# Revit family: 756-122-143-DN700-1200
name_source: partatom
category: Pipe Accessories
units: mm (PartAtom-declared; Revit-internal decimal feet)

## family parameters
Always vertical = Yes
Cut with Voids When Loaded = No
Part Type = Valve - Breaks Into
Round Connector Dimension = Use Diameter
Shared = No
Work Plane-Based = No

## types (10) — shared parameters
Body_wallthickness = 10 mm  [stored 0.0328084 ft]
D = 240 mm
D1 = 10 mm  [stored 0.0328084 ft]
DN1000-PN10 = 756-1000-1-0402200048
DN1000-PN16 = 756-1000-1-1402200048
DN1200-PN10 = 756-1200-1-0402200048
DN1200-PN16 = 756-1200-1-1402200048
DN700_PN10 = 756-0700-1-0402200048
DN700_PN16 = 756-0700-1-1402200048
DN800_PN10 = 756-0800-1-0402200048
DN800_PN16 = 756-0800-1-1402200048
DN900-PN16 = 756-0900-1-1402200048
DN900_PN10 = 756-0900-1-0402200048
Description_ = AVK DOUBLE ECC. BUTTERFLY VALVE, LONG
Disk_1 = 25 mm  [stored 0.082021 ft]
Disk_2 = 25 mm  [stored 0.082021 ft]
GB_Flange = 5 mm  [stored 0.0164042 ft]
HW_Connecting rod ref = 480 mm
HW_Dia = 20 mm  [stored 0.0656168 ft]
Offset = 3 mm  [stored 0.00984252 ft]
Pin_dia = 60 mm  [stored 0.19685 ft]
RF_Cut_Thickness = 5 mm  [stored 0.0164042 ft]
Rib_depth = 15 mm  [stored 0.0492126 ft]
Search_table = 756-122-143-DN700-1200
URL_product_pages = https://www.avkvalves.com

## per-type parameters (varying)
- DN0700_PN16: A=342 mm; A2=201.18 mm; B=615 mm; Bottom_Depth=1050.15 mm; Bottom_width=427 mm; C=297 mm; C_Rod=38 mm  [stored 0.124672 ft]; DN=700.1 mm; Disc_Dia=684 mm; Disc_width=40 mm  [stored 0.131234 ft]; Flange_OD=455 mm; Flange_Thickness=40 mm  [stored 0.131234 ft]; GB_Dia=39.75 mm  [stored 0.130413 ft]; GB_HW=95 mm; GB_Width=82 mm  [stored 0.269029 ft]; GB_Width_2=117 mm  [stored 0.383858 ft]; GB_Width_3=130 mm  [stored 0.426509 ft]; GB_Width_Ref=143.33 mm; Gear_box_Mount_Flange_width=90 mm  [stored 0.295276 ft]; Gear_box_Mount_width=85 mm  [stored 0.278871 ft]; Gear_box_depth=307 mm; H1=575.25 mm; H2=565 mm; H3=566 mm; HW_Height=1195 mm; ID (Radius)=350.05 mm; L=430 mm; L1=124 mm  [stored 0.406824 ft]; L2=130 mm  [stored 0.426509 ft]; Pin_Depth=805.05 mm; Pin_width=215 mm; Rf_Dia=397 mm; Rib_dia=37.5 mm; Rib_height=413.64 mm; Rib_height_2=120.25 mm  [stored 0.394521 ft]; Rib_width=350 mm; Rib_width_2=180 mm; W1=455 mm; W2=850 mm; W2_Ref_2=62.5 mm  [stored 0.205052 ft]; W2_ref=125 mm  [stored 0.410105 ft]; W3=527 mm; W4=537 mm; W5=1205 mm
- DN0800_PN10: A=469 mm; A2=275.88 mm; B=717 mm; Bottom_Depth=1200 mm; Bottom_width=460 mm; C=347 mm; C_Rod=38 mm  [stored 0.124672 ft]; DN=800 mm; Disc_Dia=786.5 mm; Disc_width=40 mm  [stored 0.131234 ft]; Flange_OD=507.5 mm; Flange_Thickness=40 mm  [stored 0.131234 ft]; GB_Dia=47.5 mm; GB_HW=155 mm; GB_Width=112 mm  [stored 0.367454 ft]; GB_Width_2=126 mm  [stored 0.413386 ft]; GB_Width_3=140 mm  [stored 0.459318 ft]; GB_Width_Ref=156.67 mm; Gear_box_Mount_Flange_width=90 mm  [stored 0.295276 ft]; Gear_box_Mount_width=85 mm  [stored 0.278871 ft]; Gear_box_depth=434 mm; H1=669.5 mm; H2=635 mm; H3=650 mm; HW_Height=1219 mm; ID (Radius)=400 mm; L=470 mm; L1=155 mm; L2=161 mm; Pin_Depth=907.5 mm; Pin_width=235 mm; Rf_Dia=450 mm; Rib_dia=40 mm  [stored 0.131234 ft]; Rib_height=461.36 mm; Rib_height_2=162 mm; Rib_width=390 mm; Rib_width_2=180 mm; W1=508 mm; W2=920 mm; W2_Ref_2=102 mm; W2_ref=204 mm; W3=626 mm; W4=635 mm; W5=1229 mm
- DN0800_PN16: A=469 mm; A2=275.88 mm; B=717 mm; Bottom_Depth=1200.15 mm; Bottom_width=492 mm; C=317 mm; C_Rod=38 mm  [stored 0.124672 ft]; DN=800.1 mm; Disc_Dia=786.5 mm; Disc_width=40 mm  [stored 0.131234 ft]; Flange_OD=512.5 mm; Flange_Thickness=40 mm  [stored 0.131234 ft]; GB_Dia=47.5 mm; GB_HW=155 mm; GB_Width=82 mm  [stored 0.269029 ft]; GB_Width_2=126 mm  [stored 0.413386 ft]; GB_Width_3=140 mm  [stored 0.459318 ft]; GB_Width_Ref=156.67 mm; Gear_box_Mount_Flange_width=90 mm  [stored 0.295276 ft]; Gear_box_Mount_width=85 mm  [stored 0.278871 ft]; Gear_box_depth=434 mm; H1=669.5 mm; H2=635 mm; H3=650 mm; HW_Height=1253 mm; ID (Radius)=400.05 mm; L=470 mm; L1=155 mm; L2=161 mm; Pin_Depth=912.55 mm; Pin_width=235 mm; Rf_Dia=450 mm; Rib_dia=40 mm  [stored 0.131234 ft]; Rib_height=465.91 mm; Rib_height_2=157 mm; Rib_width=390 mm; Rib_width_2=180 mm; W1=513 mm; W2=920 mm; W2_Ref_2=102 mm; W2_ref=204 mm; W3=626 mm; W4=635 mm; W5=1263 mm
- DN0900_PN10: A=469 mm; A2=275.88 mm; B=767 mm; Bottom_Depth=1350 mm; Bottom_width=524 mm; C=337 mm; C_Rod=38 mm  [stored 0.124672 ft]; DN=900 mm; Disc_Dia=886.5 mm; Disc_width=40 mm  [stored 0.131234 ft]; Flange_OD=557.5 mm; Flange_Thickness=45 mm  [stored 0.147638 ft]; GB_Dia=52.5 mm  [stored 0.172244 ft]; GB_HW=175 mm; GB_Width=82 mm  [stored 0.269029 ft]; GB_Width_2=139.5 mm; GB_Width_3=155 mm; GB_Width_Ref=170 mm; Gear_box_Mount_Flange_width=100 mm  [stored 0.328084 ft]; Gear_box_Mount_width=95 mm; Gear_box_depth=434 mm; H1=714.5 mm; H2=705 mm; H3=701 mm; HW_Height=1298 mm; ID (Radius)=450 mm; L=510 mm; L1=185 mm; L2=191 mm; Pin_Depth=1007.5 mm; Pin_width=255 mm; Rf_Dia=500 mm; Rib_dia=40 mm  [stored 0.131234 ft]; Rib_height=506.82 mm; Rib_height_2=157 mm; Rib_width=420 mm; Rib_width_2=200 mm; W1=558 mm; W2=990 mm; W2_Ref_2=102 mm; W2_ref=204 mm; W3=721 mm; W4=729 mm; W5=1308 mm
- DN0900-PN16: A=469 mm; A2=275.88 mm; B=767 mm; Bottom_Depth=1350.15 mm; Bottom_width=556 mm; C=367 mm; C_Rod=38 mm  [stored 0.124672 ft]; DN=900.1 mm; Disc_Dia=886.5 mm; Disc_width=40 mm  [stored 0.131234 ft]; Flange_OD=562 mm; Flange_Thickness=45 mm  [stored 0.147638 ft]; GB_Dia=52.5 mm  [stored 0.172244 ft]; GB_HW=175 mm; GB_Width=112 mm  [stored 0.367454 ft]; GB_Width_2=139.5 mm; GB_Width_3=155 mm; GB_Width_Ref=170 mm; Gear_box_Mount_Flange_width=100 mm  [stored 0.328084 ft]; Gear_box_Mount_width=95 mm; Gear_box_depth=434 mm; H1=714.5 mm; H2=705 mm; H3=701 mm; HW_Height=1274 mm; ID (Radius)=450.05 mm; L=510 mm; L1=185 mm; L2=191 mm; Pin_Depth=1012.05 mm; Pin_width=255 mm; Rf_Dia=500 mm; Rib_dia=40 mm  [stored 0.131234 ft]; Rib_height=510.91 mm; Rib_height_2=152.5 mm  [stored 0.500328 ft]; Rib_width=420 mm; Rib_width_2=200 mm; W1=563 mm; W2=990 mm; W2_Ref_2=102 mm; W2_ref=204 mm; W3=721 mm; W4=729 mm; W5=1284 mm
- DN1000-PN10: A=469 mm; A2=275.88 mm; B=837 mm; Bottom_Depth=1500 mm; Bottom_width=588 mm; C=306 mm; C_Rod=48 mm  [stored 0.15748 ft]; DN=1000 mm; Disc_Dia=986 mm; Disc_width=50 mm  [stored 0.164042 ft]; Flange_OD=615 mm; Flange_Thickness=50 mm  [stored 0.164042 ft]; GB_Dia=55 mm  [stored 0.180446 ft]; GB_HW=203.5 mm; GB_Width=31 mm  [stored 0.101706 ft]; GB_Width_2=157.5 mm; GB_Width_3=175 mm; GB_Width_Ref=183.33 mm; Gear_box_Mount_Flange_width=110 mm  [stored 0.360892 ft]; Gear_box_Mount_width=105 mm  [stored 0.344488 ft]; Gear_box_depth=434 mm; H1=782 mm; H2=785 mm; H3=771 mm; HW_Height=1482 mm; ID (Radius)=500 mm; L=550 mm; L1=215 mm; L2=221 mm; Pin_Depth=1115 mm; Pin_width=275 mm; Rf_Dia=556 mm; Rib_dia=40 mm  [stored 0.131234 ft]; Rib_height=559.09 mm; Rib_height_2=167 mm; Rib_width=450 mm; Rib_width_2=220 mm; W1=615 mm; W2=1086 mm; W2_Ref_2=102 mm; W2_ref=204 mm; W3=814 mm; W4=822 mm; W5=1492 mm
- DN1000-PN16: A=469 mm; A2=275.88 mm; B=837 mm; Bottom_Depth=1500.15 mm; Bottom_width=620 mm; C=306 mm; C_Rod=48 mm  [stored 0.15748 ft]; DN=1000.1 mm; Disc_Dia=986 mm; Disc_width=50 mm  [stored 0.164042 ft]; Flange_OD=627.5 mm; Flange_Thickness=50 mm  [stored 0.164042 ft]; GB_Dia=55 mm  [stored 0.180446 ft]; GB_HW=203.5 mm; GB_Width=31 mm  [stored 0.101706 ft]; GB_Width_2=157.5 mm; GB_Width_3=175 mm; GB_Width_Ref=183.33 mm; Gear_box_Mount_Flange_width=110 mm  [stored 0.360892 ft]; Gear_box_Mount_width=105 mm  [stored 0.344488 ft]; Gear_box_depth=434 mm; H1=782 mm; H2=785 mm; H3=771 mm; HW_Height=1495 mm; ID (Radius)=500.05 mm; L=550 mm; L1=215 mm; L2=221 mm; Pin_Depth=1127.55 mm; Pin_width=275 mm; Rf_Dia=556 mm; Rib_dia=40 mm  [stored 0.131234 ft]; Rib_height=570.45 mm; Rib_height_2=154.5 mm; Rib_width=450 mm; Rib_width_2=220 mm; W1=628 mm; W2=1086 mm; W2_Ref_2=102 mm; W2_ref=204 mm; W3=814 mm; W4=822 mm; W5=1505 mm
- DN1200-PN10: A=505 mm; A2=297.06 mm; B=957 mm; Bottom_Depth=1800 mm; Bottom_width=653 mm; C=346 mm; C_Rod=48 mm  [stored 0.15748 ft]; DN=1200 mm; Disc_Dia=1172.5 mm; Disc_width=50 mm  [stored 0.164042 ft]; Flange_OD=727.5 mm; Flange_Thickness=60 mm  [stored 0.19685 ft]; GB_Dia=60 mm  [stored 0.19685 ft]; GB_HW=260 mm; GB_Width=31 mm  [stored 0.101706 ft]; GB_Width_2=175.5 mm; GB_Width_3=195 mm; GB_Width_Ref=210 mm; Gear_box_Mount_Flange_width=125 mm  [stored 0.410105 ft]; Gear_box_Mount_width=120 mm  [stored 0.393701 ft]; Gear_box_depth=470 mm; H1=897 mm; H2=874 mm; H3=899 mm; HW_Height=1595 mm; ID (Radius)=600 mm; L=630 mm; L1=268 mm; L2=274 mm; Pin_Depth=1327.5 mm; Pin_width=315 mm; Rf_Dia=666 mm; Rib_dia=40 mm  [stored 0.131234 ft]; Rib_height=661.36 mm; Rib_height_2=169.5 mm; Rib_width=510 mm; Rib_width_2=250 mm; W1=728 mm; W2=1171 mm; W2_Ref_2=102 mm; W2_ref=204 mm; W3=985 mm; W4=993 mm; W5=1605 mm
- DN1200-PN16: A=505 mm; A2=297.06 mm; B=957 mm; Bottom_Depth=1800.15 mm; Bottom_width=685 mm; C=346 mm; C_Rod=48 mm  [stored 0.15748 ft]; DN=1200.1 mm; Disc_Dia=1172.5 mm; Disc_width=50 mm  [stored 0.164042 ft]; Flange_OD=742.5 mm; Flange_Thickness=60 mm  [stored 0.19685 ft]; GB_Dia=60 mm  [stored 0.19685 ft]; GB_HW=260 mm; GB_Width=31 mm  [stored 0.101706 ft]; GB_Width_2=175.5 mm; GB_Width_3=195 mm; GB_Width_Ref=210 mm; Gear_box_Mount_Flange_width=125 mm  [stored 0.410105 ft]; Gear_box_Mount_width=120 mm  [stored 0.393701 ft]; Gear_box_depth=470 mm; H1=897 mm; H2=874 mm; H3=899 mm; HW_Height=1610 mm; ID (Radius)=600.05 mm; L=630 mm; L1=268 mm; L2=274 mm; Pin_Depth=1342.55 mm; Pin_width=315 mm; Rf_Dia=666 mm; Rib_dia=40 mm  [stored 0.131234 ft]; Rib_height=675 mm; Rib_height_2=154.5 mm; Rib_width=510 mm; Rib_width_2=250 mm; W1=743 mm; W2=1171 mm; W2_Ref_2=102 mm; W2_ref=204 mm; W3=985 mm; W4=993 mm; W5=1620 mm
- DN0700_PN10: A=342 mm; A2=201.18 mm; B=615 mm; Bottom_Depth=1050 mm; Bottom_width=395 mm; C=255 mm; C_Rod=38 mm  [stored 0.124672 ft]; DN=700 mm; Disc_Dia=684 mm; Disc_width=40 mm  [stored 0.131234 ft]; Flange_OD=447.5 mm; Flange_Thickness=40 mm  [stored 0.131234 ft]; GB_Dia=39.75 mm  [stored 0.130413 ft]; GB_HW=95 mm; GB_Width=40 mm  [stored 0.131234 ft]; GB_Width_2=117 mm  [stored 0.383858 ft]; GB_Width_3=130 mm  [stored 0.426509 ft]; GB_Width_Ref=143.33 mm; Gear_box_Mount_Flange_width=90 mm  [stored 0.295276 ft]; Gear_box_Mount_width=85 mm  [stored 0.278871 ft]; Gear_box_depth=307 mm; H1=575.25 mm; H2=565 mm; H3=566 mm; HW_Height=1181 mm; ID (Radius)=350 mm; L=430 mm; L1=124 mm  [stored 0.406824 ft]; L2=130 mm  [stored 0.426509 ft]; Pin_Depth=797.5 mm; Pin_width=215 mm; Rf_Dia=397 mm; Rib_dia=37.5 mm; Rib_height=406.82 mm; Rib_height_2=127.75 mm  [stored 0.419127 ft]; Rib_width=350 mm; Rib_width_2=180 mm; W1=448 mm; W2=846 mm; W2_Ref_2=62.5 mm  [stored 0.205052 ft]; W2_ref=125 mm  [stored 0.410105 ft]; W3=527 mm; W4=537 mm; W5=1191 mm

note: [stored X ft] marks values corroborated as IEEE doubles in the binary element streams (Revit-internal decimal feet)

## geometry (parser evidence)
native form markers: Sweep x11
no freeform markers — native parametric forms only
